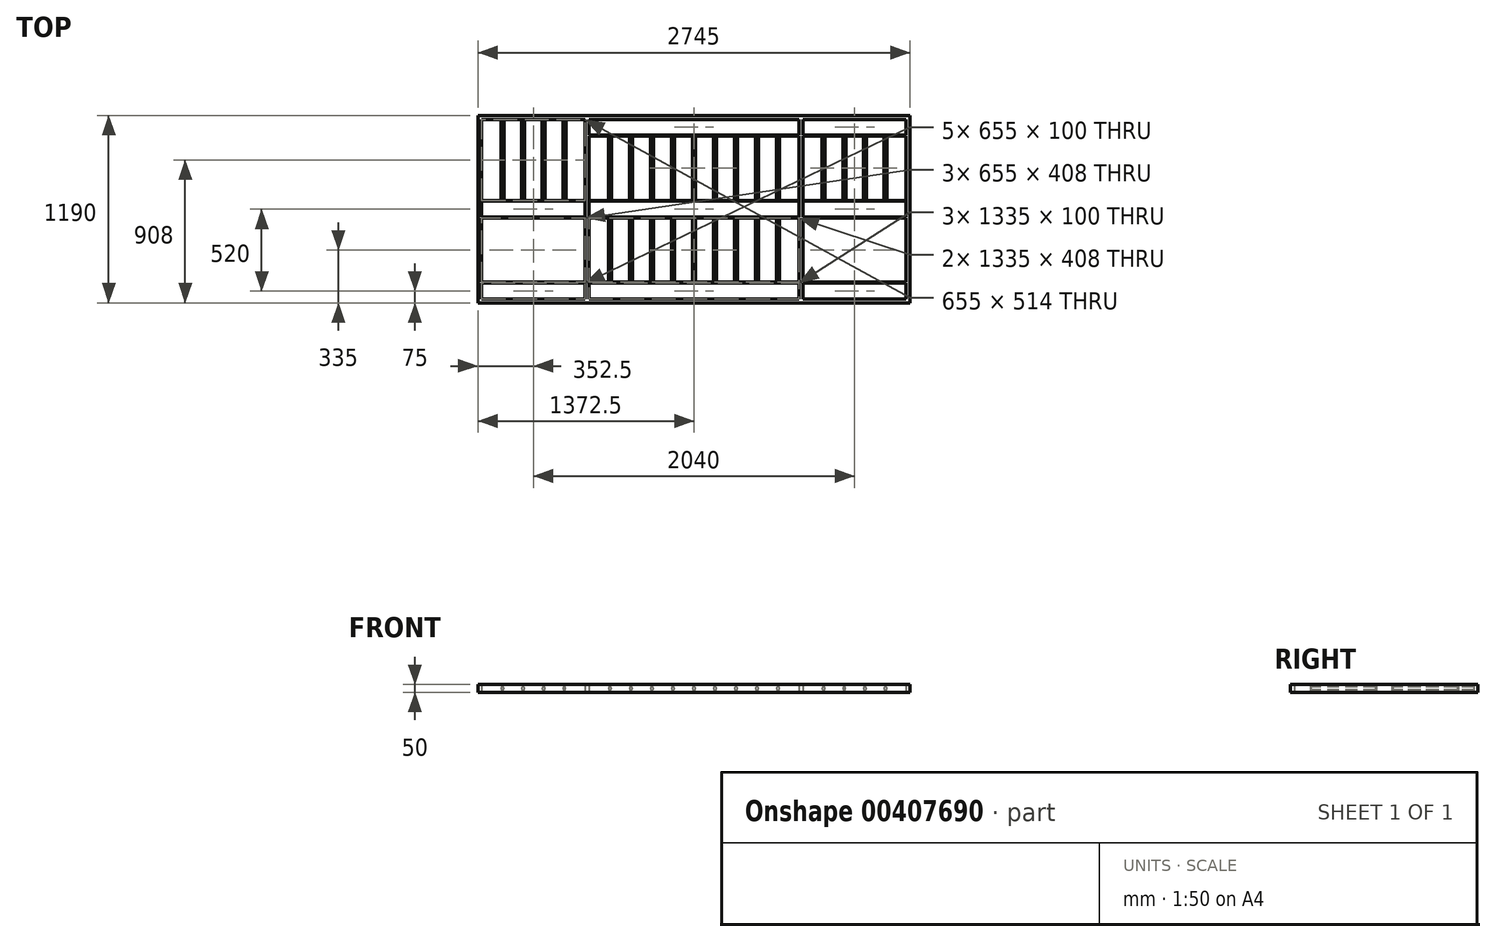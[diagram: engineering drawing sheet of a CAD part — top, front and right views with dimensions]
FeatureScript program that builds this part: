
annotation { "Feature Type Name" : "Feature", "Feature Type Description" : "" }
export const myFeature = defineFeature(function(context is Context, id is Id, definition is map)
    precondition{}
    {
        {
            var Q0;
            Q0=qCreatedBy(makeId("Top.planeOp"),FACE);
            var sketch = newSketch(context, id + "F0", { "sketchPlane" : qUnion([Q0])});
            skLineSegment(sketch, "E0.bottom", {"start": v(0, 0) * mm, "end": v(705, 0) * mm});
            skLineSegment(sketch, "E0.top", {"start": v(0, 1190) * mm, "end": v(705, 1190) * mm});
            skLineSegment(sketch, "E0.left", {"start": v(0, 0) * mm, "end": v(0, 1190) * mm});
            skLineSegment(sketch, "E0.right", {"start": v(705, 0) * mm, "end": v(705, 1190) * mm});
            skLineSegment(sketch, "E1.0", {"start": v(25, 1165) * mm, "end": v(680, 1165) * mm});
            skLineSegment(sketch, "E1.1", {"start": v(25, 25) * mm, "end": v(25, 1165) * mm});
            skLineSegment(sketch, "E1.2", {"start": v(25, 25) * mm, "end": v(680, 25) * mm});
            skLineSegment(sketch, "E1.3", {"start": v(680, 25) * mm, "end": v(680, 1165) * mm});
            skLineSegment(sketch, "E2", {"start": v(759.37, 595) * mm, "end": v(-360.82, 595) * mm, "construction": true});
            skLineSegment(sketch, "E3.bottom", {"start": v(25, 125) * mm, "end": v(680, 125) * mm});
            skLineSegment(sketch, "E3.top", {"start": v(25, 131) * mm, "end": v(680, 131) * mm});
            skLineSegment(sketch, "E3.left", {"start": v(25, 125) * mm, "end": v(25, 131) * mm});
            skLineSegment(sketch, "E3.right", {"start": v(680, 125) * mm, "end": v(680, 131) * mm});
            skLineSegment(sketch, "E4.bottom", {"start": v(25, 545) * mm, "end": v(680, 545) * mm});
            skLineSegment(sketch, "E4.top", {"start": v(25, 539) * mm, "end": v(680, 539) * mm});
            skLineSegment(sketch, "E4.left", {"start": v(25, 545) * mm, "end": v(25, 539) * mm});
            skLineSegment(sketch, "E4.right", {"start": v(680, 545) * mm, "end": v(680, 539) * mm});
            skLineSegment(sketch, "E5.MirrorCS", {"start": v(25, 645) * mm, "end": v(680, 645) * mm});
            skLineSegment(sketch, "E6.MirrorCS", {"start": v(25, 651) * mm, "end": v(680, 651) * mm});
            skLineSegment(sketch, "E7.MirrorCS", {"start": v(25, 1065) * mm, "end": v(25, 1059) * mm});
            skLineSegment(sketch, "E8.MirrorCS", {"start": v(680, 1065) * mm, "end": v(680, 1059) * mm});
            skLineSegment(sketch, "E9.MirrorCS", {"start": v(25, 1059) * mm, "end": v(680, 1059) * mm});
            skLineSegment(sketch, "E10.MirrorCS", {"start": v(25, 1065) * mm, "end": v(680, 1065) * mm});
            skLineSegment(sketch, "E11.1.0.0", {"start": v(705, 1165) * mm, "end": v(1360, 1165) * mm});
            skLineSegment(sketch, "E11.1.0.1", {"start": v(705, 1065) * mm, "end": v(1360, 1065) * mm});
            skLineSegment(sketch, "E11.1.0.2", {"start": v(680, 1190) * mm, "end": v(1385, 1190) * mm});
            skLineSegment(sketch, "E11.1.0.3", {"start": v(705, 545) * mm, "end": v(1360, 545) * mm});
            skLineSegment(sketch, "E11.1.0.4", {"start": v(705, 131) * mm, "end": v(1360, 131) * mm});
            skLineSegment(sketch, "E11.1.0.5", {"start": v(705, 651) * mm, "end": v(1360, 651) * mm});
            skLineSegment(sketch, "E11.1.0.6", {"start": v(705, 1059) * mm, "end": v(1360, 1059) * mm});
            skLineSegment(sketch, "E11.1.0.7", {"start": v(680, 0) * mm, "end": v(1385, 0) * mm});
            skLineSegment(sketch, "E11.1.0.8", {"start": v(1360, 25) * mm, "end": v(1360, 1165) * mm, "construction": true});
            skLineSegment(sketch, "E11.1.0.9", {"start": v(705, 539) * mm, "end": v(1360, 539) * mm});
            skLineSegment(sketch, "E11.1.0.10", {"start": v(705, 125) * mm, "end": v(1360, 125) * mm});
            skLineSegment(sketch, "E11.1.0.11", {"start": v(1439.37, 595) * mm, "end": v(319.18, 595) * mm, "construction": true});
            skLineSegment(sketch, "E11.1.0.12", {"start": v(705, 25) * mm, "end": v(1360, 25) * mm});
            skLineSegment(sketch, "E11.1.0.13", {"start": v(1385, 0) * mm, "end": v(1385, 1190) * mm, "construction": true});
            skLineSegment(sketch, "E11.1.0.14", {"start": v(705, 645) * mm, "end": v(1360, 645) * mm});
            skLineSegment(sketch, "E11.1.0.15", {"start": v(1360, 1065) * mm, "end": v(1360, 1059) * mm});
            skLineSegment(sketch, "E11.1.0.16", {"start": v(1360, 545) * mm, "end": v(1360, 539) * mm});
            skLineSegment(sketch, "E11.1.0.17", {"start": v(1360, 125) * mm, "end": v(1360, 131) * mm});
            skLineSegment(sketch, "E11.2.0.0", {"start": v(1385, 1165) * mm, "end": v(2040, 1165) * mm});
            skLineSegment(sketch, "E11.2.0.1", {"start": v(1385, 1065) * mm, "end": v(2040, 1065) * mm});
            skLineSegment(sketch, "E11.2.0.2", {"start": v(1360, 1190) * mm, "end": v(2065, 1190) * mm});
            skLineSegment(sketch, "E11.2.0.3", {"start": v(1385, 545) * mm, "end": v(2040, 545) * mm});
            skLineSegment(sketch, "E11.2.0.4", {"start": v(1385, 131) * mm, "end": v(2040, 131) * mm});
            skLineSegment(sketch, "E11.2.0.5", {"start": v(1385, 651) * mm, "end": v(2040, 651) * mm});
            skLineSegment(sketch, "E11.2.0.6", {"start": v(1385, 1059) * mm, "end": v(2040, 1059) * mm});
            skLineSegment(sketch, "E11.2.0.7", {"start": v(1360, 0) * mm, "end": v(2065, 0) * mm});
            skLineSegment(sketch, "E11.2.0.8", {"start": v(2040, 25) * mm, "end": v(2040, 1165) * mm});
            skLineSegment(sketch, "E11.2.0.9", {"start": v(1385, 539) * mm, "end": v(2040, 539) * mm});
            skLineSegment(sketch, "E11.2.0.10", {"start": v(1385, 125) * mm, "end": v(2040, 125) * mm});
            skLineSegment(sketch, "E11.2.0.11", {"start": v(2119.37, 595) * mm, "end": v(999.18, 595) * mm, "construction": true});
            skLineSegment(sketch, "E11.2.0.12", {"start": v(1385, 25) * mm, "end": v(2040, 25) * mm});
            skLineSegment(sketch, "E11.2.0.13", {"start": v(2065, 0) * mm, "end": v(2065, 1190) * mm});
            skLineSegment(sketch, "E11.2.0.14", {"start": v(1385, 645) * mm, "end": v(2040, 645) * mm});
            skLineSegment(sketch, "E11.2.0.15", {"start": v(2040, 1065) * mm, "end": v(2040, 1059) * mm});
            skLineSegment(sketch, "E11.2.0.16", {"start": v(2040, 545) * mm, "end": v(2040, 539) * mm});
            skLineSegment(sketch, "E11.2.0.17", {"start": v(2040, 125) * mm, "end": v(2040, 131) * mm});
            skLineSegment(sketch, "E11.direction1", {"start": v(0, 0) * mm, "end": v(680, 0) * mm, "construction": true});
            skLineSegment(sketch, "E12.0.3.0", {"start": v(2065, 1165) * mm, "end": v(2720, 1165) * mm});
            skLineSegment(sketch, "E12.3.3.0", {"start": v(2065, 1065) * mm, "end": v(2720, 1065) * mm});
            skLineSegment(sketch, "E12.6.3.0", {"start": v(2040, 1190) * mm, "end": v(2745, 1190) * mm});
            skLineSegment(sketch, "E12.9.3.0", {"start": v(2065, 545) * mm, "end": v(2720, 545) * mm});
            skLineSegment(sketch, "E12.12.3.0", {"start": v(2065, 131) * mm, "end": v(2720, 131) * mm});
            skLineSegment(sketch, "E12.15.3.0", {"start": v(2065, 651) * mm, "end": v(2720, 651) * mm});
            skLineSegment(sketch, "E12.18.3.0", {"start": v(2065, 1059) * mm, "end": v(2720, 1059) * mm});
            skLineSegment(sketch, "E12.21.3.0", {"start": v(2040, 0) * mm, "end": v(2745, 0) * mm});
            skLineSegment(sketch, "E12.24.3.0", {"start": v(2720, 25) * mm, "end": v(2720, 1165) * mm});
            skLineSegment(sketch, "E12.27.3.0", {"start": v(2065, 539) * mm, "end": v(2720, 539) * mm});
            skLineSegment(sketch, "E12.30.3.0", {"start": v(2065, 125) * mm, "end": v(2720, 125) * mm});
            skLineSegment(sketch, "E12.33.3.0", {"start": v(2799.37, 595) * mm, "end": v(1679.18, 595) * mm, "construction": true});
            skLineSegment(sketch, "E12.36.3.0", {"start": v(2065, 25) * mm, "end": v(2720, 25) * mm});
            skLineSegment(sketch, "E12.39.3.0", {"start": v(2745, 0) * mm, "end": v(2745, 1190) * mm});
            skLineSegment(sketch, "E12.42.3.0", {"start": v(2065, 645) * mm, "end": v(2720, 645) * mm});
            skLineSegment(sketch, "E12.45.3.0", {"start": v(2720, 1065) * mm, "end": v(2720, 1059) * mm});
            skLineSegment(sketch, "E12.48.3.0", {"start": v(2720, 545) * mm, "end": v(2720, 539) * mm});
            skLineSegment(sketch, "E12.51.3.0", {"start": v(2720, 125) * mm, "end": v(2720, 131) * mm});
            skLineSegment(sketch, "E13.bottom", {"start": v(1360, 539) * mm, "end": v(1385, 539) * mm});
            skLineSegment(sketch, "E13.top", {"start": v(1360, 545) * mm, "end": v(1385, 545) * mm});
            skLineSegment(sketch, "E13.left", {"start": v(1360, 539) * mm, "end": v(1360, 545) * mm});
            skLineSegment(sketch, "E13.right", {"start": v(1385, 539) * mm, "end": v(1385, 545) * mm});
            skLineSegment(sketch, "E14.bottom", {"start": v(1360, 125) * mm, "end": v(1385, 125) * mm});
            skLineSegment(sketch, "E14.top", {"start": v(1360, 131) * mm, "end": v(1385, 131) * mm});
            skLineSegment(sketch, "E14.right", {"start": v(1385, 125) * mm, "end": v(1385, 131) * mm});
            skLineSegment(sketch, "E15.bottom", {"start": v(1385, 1065) * mm, "end": v(1360, 1065) * mm});
            skLineSegment(sketch, "E15.top", {"start": v(1385, 1059) * mm, "end": v(1360, 1059) * mm});
            skLineSegment(sketch, "E15.left", {"start": v(1385, 1065) * mm, "end": v(1385, 1059) * mm});
            skLineSegment(sketch, "E16.bottom", {"start": v(1385, 645) * mm, "end": v(1360, 645) * mm});
            skLineSegment(sketch, "E16.top", {"start": v(1385, 651) * mm, "end": v(1360, 651) * mm});
            skLineSegment(sketch, "E16.left", {"start": v(1385, 645) * mm, "end": v(1385, 651) * mm});
            skLineSegment(sketch, "E16.right", {"start": v(1360, 645) * mm, "end": v(1360, 651) * mm});
            skLineSegment(sketch, "E17", {"start": v(1360, 1165) * mm, "end": v(1385, 1165) * mm});
            skLineSegment(sketch, "E18", {"start": v(1360, 25) * mm, "end": v(1385, 25) * mm});
            skSolve(sketch);
        }
        {
            var Q0;
            Q0=qSketchRegion(id+"F0",true);
            var Q1;
            Q1=makeQuery(id+"F0.imprint","IMPRINT",FACE,{"disambiguationData":[TD([[makeQuery(id+"F0.imprint","IMPRINT",EDGE,{"derivedFrom":sQuery(id+"F0.wireOp",EDGE,"E4.bottom")}),-1.0]])]});
            var Q2;
            Q2=makeQuery(id+"F0.imprint","IMPRINT",FACE,{"disambiguationData":[TD([[makeQuery(id+"F0.imprint","IMPRINT",EDGE,{"derivedFrom":sQuery(id+"F0.wireOp",EDGE,"baab227e-6a5d-40b9-91ee-7446e1ab67f20.MirrorCS")}),1.0]])]});
            var Q3;
            Q3=makeQuery(id+"F0.imprint","IMPRINT",FACE,{"disambiguationData":[TD([[makeQuery(id+"F0.imprint","IMPRINT",EDGE,{"derivedFrom":sQuery(id+"F0.wireOp",EDGE,"E3.bottom")}),1.0]])]});
            var Q4;
            Q4=makeQuery(id+"F0.imprint","IMPRINT",FACE,{"disambiguationData":[TD([[makeQuery(id+"F0.imprint","IMPRINT",EDGE,{"derivedFrom":sQuery(id+"F0.wireOp",EDGE,"TbBb99Yr-0gyQ-v6ej-gQRB-Bgt5jI2MECaT.bottom")}),-1.0]])]});
            var Q5;
            Q5=makeQuery(id+"F0.imprint","IMPRINT",FACE,{"disambiguationData":[TD([[makeQuery(id+"F0.imprint","IMPRINT",EDGE,{"derivedFrom":sQuery(id+"F0.wireOp",EDGE,"NzViuoU3-R4T5-xjC5-rI0y-QMhb7gm5c65x.bottom")}),-1.0]])]});
            var Q6;
            Q6=makeQuery(id+"F0.imprint","IMPRINT",FACE,{"disambiguationData":[TD([[makeQuery(id+"F0.imprint","IMPRINT",EDGE,{"derivedFrom":sQuery(id+"F0.wireOp",EDGE,"baab227e-6a5d-40b9-91ee-7446e1ab67f23.MirrorCS")}),-1.0]])]});
            var Q7;
            Q7=makeQuery(id+"F0.imprint","IMPRINT",FACE,{"disambiguationData":[TD([[makeQuery(id+"F0.imprint","IMPRINT",EDGE,{"derivedFrom":sQuery(id+"F0.wireOp",EDGE,"baab227e-6a5d-40b9-91ee-7446e1ab67f22.MirrorCS")}),-1.0]])]});
            var Q8;
            Q8=makeQuery(id+"F0.imprint","IMPRINT",FACE,{"disambiguationData":[TD([[makeQuery(id+"F0.imprint","IMPRINT",EDGE,{"derivedFrom":sQuery(id+"F0.wireOp",EDGE,"baab227e-6a5d-40b9-91ee-7446e1ab67f21.MirrorCS")}),1.0]])]});
            var Q9;
            {var subQ0=sQuery(id+"F0.wireOp",EDGE,"E5.MirrorCS");Q9=makeQuery(id+"F0.imprint","IMPRINT",FACE,{"disambiguationData":[TD([[makeQuery(id+"F0.imprint","IMPRINT",EDGE,{"derivedFrom":subQ0}),1.0]])]});}
            var Q10;
            Q10=makeQuery(id+"F0.imprint","IMPRINT",FACE,{"disambiguationData":[TD([[makeQuery(id+"F0.imprint","IMPRINT",EDGE,{"derivedFrom":sQuery(id+"F0.wireOp",EDGE,"E7.MirrorCS")}),1.0]])]});
            var Q11;
            {var subQ0=sQuery(id+"F0.wireOp",EDGE,"E11.1.0.5");Q11=makeQuery(id+"F0.imprint","IMPRINT",FACE,{"disambiguationData":[TD([[makeQuery(id+"F0.imprint","IMPRINT",EDGE,{"derivedFrom":subQ0}),-1.0]])]});}
            var Q12;
            {var subQ0=sQuery(id+"F0.wireOp",EDGE,"E11.2.0.5");Q12=makeQuery(id+"F0.imprint","IMPRINT",FACE,{"disambiguationData":[TD([[makeQuery(id+"F0.imprint","IMPRINT",EDGE,{"derivedFrom":subQ0}),-1.0]])]});}
            var Q13;
            {var subQ0=sQuery(id+"F0.wireOp",EDGE,"E11.2.0.3");Q13=makeQuery(id+"F0.imprint","IMPRINT",FACE,{"disambiguationData":[TD([[makeQuery(id+"F0.imprint","IMPRINT",EDGE,{"derivedFrom":subQ0}),-1.0]])]});}
            var Q14;
            {var subQ0=sQuery(id+"F0.wireOp",EDGE,"E11.1.0.3");Q14=makeQuery(id+"F0.imprint","IMPRINT",FACE,{"disambiguationData":[TD([[makeQuery(id+"F0.imprint","IMPRINT",EDGE,{"derivedFrom":subQ0}),-1.0]])]});}
            var Q15;
            {var subQ0=sQuery(id+"F0.wireOp",EDGE,"E12.9.3.0");Q15=makeQuery(id+"F0.imprint","IMPRINT",FACE,{"disambiguationData":[TD([[makeQuery(id+"F0.imprint","IMPRINT",EDGE,{"derivedFrom":subQ0}),-1.0]])]});}
            var Q16;
            {var subQ0=sQuery(id+"F0.wireOp",EDGE,"E12.15.3.0");Q16=makeQuery(id+"F0.imprint","IMPRINT",FACE,{"disambiguationData":[TD([[makeQuery(id+"F0.imprint","IMPRINT",EDGE,{"derivedFrom":subQ0}),-1.0]])]});}
            var Q17;
            {var subQ0=sQuery(id+"F0.wireOp",EDGE,"E12.3.3.0");Q17=makeQuery(id+"F0.imprint","IMPRINT",FACE,{"disambiguationData":[TD([[makeQuery(id+"F0.imprint","IMPRINT",EDGE,{"derivedFrom":subQ0}),-1.0]])]});}
            var Q18;
            {var subQ0=sQuery(id+"F0.wireOp",EDGE,"E11.2.0.1");Q18=makeQuery(id+"F0.imprint","IMPRINT",FACE,{"disambiguationData":[TD([[makeQuery(id+"F0.imprint","IMPRINT",EDGE,{"derivedFrom":subQ0}),-1.0]])]});}
            var Q19;
            {var subQ0=sQuery(id+"F0.wireOp",EDGE,"E11.1.0.1");Q19=makeQuery(id+"F0.imprint","IMPRINT",FACE,{"disambiguationData":[TD([[makeQuery(id+"F0.imprint","IMPRINT",EDGE,{"derivedFrom":subQ0}),-1.0]])]});}
            var Q20;
            {var subQ0=sQuery(id+"F0.wireOp",EDGE,"E12.12.3.0");Q20=makeQuery(id+"F0.imprint","IMPRINT",FACE,{"disambiguationData":[TD([[makeQuery(id+"F0.imprint","IMPRINT",EDGE,{"derivedFrom":subQ0}),-1.0]])]});}
            var Q21;
            {var subQ0=sQuery(id+"F0.wireOp",EDGE,"E11.1.0.4");Q21=makeQuery(id+"F0.imprint","IMPRINT",FACE,{"disambiguationData":[TD([[makeQuery(id+"F0.imprint","IMPRINT",EDGE,{"derivedFrom":subQ0}),-1.0]])]});}
            var Q22;
            {var subQ0=sQuery(id+"F0.wireOp",EDGE,"E11.2.0.4");Q22=makeQuery(id+"F0.imprint","IMPRINT",FACE,{"disambiguationData":[TD([[makeQuery(id+"F0.imprint","IMPRINT",EDGE,{"derivedFrom":subQ0}),-1.0]])]});}
            var Q23;
            Q23=makeQuery(id+"F0.imprint","IMPRINT",FACE,{"disambiguationData":[TD([[makeQuery(id+"F0.imprint","IMPRINT",EDGE,{"derivedFrom":sQuery(id+"F0.wireOp",EDGE,"E14.bottom")}),1.0]])]});
            var Q24;
            Q24=makeQuery(id+"F0.imprint","IMPRINT",FACE,{"disambiguationData":[TD([[makeQuery(id+"F0.imprint","IMPRINT",EDGE,{"derivedFrom":sQuery(id+"F0.wireOp",EDGE,"E13.bottom")}),1.0]])]});
            var Q25;
            Q25=makeQuery(id+"F0.imprint","IMPRINT",FACE,{"disambiguationData":[TD([[makeQuery(id+"F0.imprint","IMPRINT",EDGE,{"derivedFrom":sQuery(id+"F0.wireOp",EDGE,"E15.bottom")}),1.0]])]});
            var Q26;
            Q26=makeQuery(id+"F0.imprint","IMPRINT",FACE,{"disambiguationData":[TD([[makeQuery(id+"F0.imprint","IMPRINT",EDGE,{"derivedFrom":sQuery(id+"F0.wireOp",EDGE,"E16.bottom")}),-1.0]])]});
            extrude(context, id + "F1", {"entities" : qUnion([Q0, Q1, Q2, Q3, Q4, Q5, Q6, Q7, Q8, Q9, Q10, Q11, Q12, Q13, Q14, Q15, Q16, Q17, Q18, Q19, Q20, Q21, Q22, Q23, Q24, Q25, Q26]), "depth" : 50 * mm});
        }
        {
            var Q0;
            Q0=makeQuery(id+"F1.opExtrude","SWEPT_FACE",FACE,{"disambiguationData":[OSD([sQuery(id+"F0.wireOp",EDGE,"E3.top")])]});
            var sketch = newSketch(context, id + "F2", { "sketchPlane" : qUnion([Q0])});
            skLineSegment(sketch, "E19", {"start": v(-25, 25) * mm, "end": v(-680, 25) * mm, "construction": true});
            skCircle(sketch, "E20", {"center": v(-156, 25) * mm, "radius": 9.53 * mm});
            skCircle(sketch, "E21.1.0.0", {"center": v(-287, 25) * mm, "radius": 9.53 * mm});
            skCircle(sketch, "E21.2.0.0", {"center": v(-418, 25) * mm, "radius": 9.53 * mm});
            skCircle(sketch, "E21.3.0.0", {"center": v(-549, 25) * mm, "radius": 9.53 * mm});
            skLineSegment(sketch, "E21.direction1", {"start": v(-156, 25) * mm, "end": v(-287, 25) * mm, "construction": true});
            skLineSegment(sketch, "E22", {"start": v(-680, 25) * mm, "end": v(-2065, 25) * mm, "construction": true});
            skLineSegment(sketch, "E23", {"start": v(-1372.5, 25) * mm, "end": v(-1372.5, 237.59) * mm, "construction": true});
            skCircle(sketch, "E24.MirrorC", {"center": v(-2589, 25) * mm, "radius": 9.53 * mm});
            skCircle(sketch, "E25.MirrorC", {"center": v(-2458, 25) * mm, "radius": 9.53 * mm});
            skCircle(sketch, "E26.MirrorC", {"center": v(-2327, 25) * mm, "radius": 9.53 * mm});
            skCircle(sketch, "E27.MirrorC", {"center": v(-2196, 25) * mm, "radius": 9.53 * mm});
            skSolve(sketch);
        }
        {
            var Q0;
            Q0=sQuery(id+"F2.wireOp",EDGE,"E21.2.0.0");
            var Q1;
            Q1=sQuery(id+"F2.wireOp",EDGE,"E21.3.0.0");
            var Q2;
            Q2=sQuery(id+"F2.wireOp",EDGE,"E26.MirrorC");
            var Q3;
            Q3=sQuery(id+"F2.wireOp",EDGE,"E21.1.0.0");
            var Q4;
            Q4=sQuery(id+"F2.wireOp",EDGE,"E25.MirrorC");
            var Q5;
            Q5=sQuery(id+"F2.wireOp",EDGE,"E20");
            var Q6;
            Q6=sQuery(id+"F2.wireOp",EDGE,"E27.MirrorC");
            var Q7;
            Q7=sQuery(id+"F2.wireOp",EDGE,"E24.MirrorC");
            extrude(context, id + "F3", {"bodyType" : ToolBodyType.SURFACE, "surfaceEntities" : qUnion([Q0, Q1, Q2, Q3, Q4, Q5, Q6, Q7]), "endBound" : BoundingType.UP_TO_NEXT, "depth" : 25 * mm});
        }
        {
            var Q0;
            Q0=makeQuery(id+"F1.opExtrude","SWEPT_FACE",FACE,{"disambiguationData":[OSD([sQuery(id+"F0.wireOp",EDGE,"E6.MirrorCS")])]});
            var sketch = newSketch(context, id + "F4", { "sketchPlane" : qUnion([Q0])});
            skLineSegment(sketch, "E28", {"start": v(-25, 25) * mm, "end": v(-680, 25) * mm, "construction": true});
            skLineSegment(sketch, "E29", {"start": v(-680, 25) * mm, "end": v(-2065, 25) * mm, "construction": true});
            skCircle(sketch, "E30", {"center": v(-156, 25) * mm, "radius": 9.53 * mm});
            skCircle(sketch, "E31.1.0.0", {"center": v(-287, 25) * mm, "radius": 9.53 * mm});
            skCircle(sketch, "E31.2.0.0", {"center": v(-418, 25) * mm, "radius": 9.53 * mm});
            skCircle(sketch, "E31.3.0.0", {"center": v(-549, 25) * mm, "radius": 9.53 * mm});
            skLineSegment(sketch, "E31.direction1", {"start": v(-156, 25) * mm, "end": v(-287, 25) * mm, "construction": true});
            skLineSegment(sketch, "E32", {"start": v(-1372.5, 25) * mm, "end": v(-1372.5, -85.74) * mm, "construction": true});
            skPoint(sketch, "E32.endSnap0", {"position": v(-1372.5, 25) * mm});
            skCircle(sketch, "E33.MirrorC", {"center": v(-2196, 25) * mm, "radius": 9.53 * mm});
            skCircle(sketch, "E34.MirrorC", {"center": v(-2327, 25) * mm, "radius": 9.53 * mm});
            skCircle(sketch, "E35.MirrorC", {"center": v(-2458, 25) * mm, "radius": 9.53 * mm});
            skCircle(sketch, "E36.MirrorC", {"center": v(-2589, 25) * mm, "radius": 9.53 * mm});
            skSolve(sketch);
        }
        {
            var Q0;
            Q0 = qSketchRegion(id + "F4", true);
            extrude(context, id + "F5", {"entities" : qUnion([Q0]), "operationType" : NewBodyOperationType.ADD, "endBound" : BoundingType.UP_TO_NEXT, "depth" : 25 * mm});
        }
        {
            var Q0;
            Q0=makeQuery(id+"F1.opExtrude","SWEPT_FACE",FACE,{"disambiguationData":[OSD([sQuery(id+"F0.wireOp",EDGE,"E11.1.0.4"),sQuery(id+"F0.wireOp",EDGE,"E11.2.0.4"),sQuery(id+"F0.wireOp",EDGE,"E14.top")])]});
            var sketch = newSketch(context, id + "F6", { "sketchPlane" : qUnion([Q0])});
            skLineSegment(sketch, "E37", {"start": v(-705, 25) * mm, "end": v(-2040, 25) * mm, "construction": true});
            skCircle(sketch, "E38", {"center": v(-838.5, 25) * mm, "radius": 9.53 * mm});
            skCircle(sketch, "E39.1.0.0", {"center": v(-972, 25) * mm, "radius": 9.53 * mm});
            skCircle(sketch, "E39.2.0.0", {"center": v(-1105.5, 25) * mm, "radius": 9.53 * mm});
            skCircle(sketch, "E39.3.0.0", {"center": v(-1239, 25) * mm, "radius": 9.53 * mm});
            skCircle(sketch, "E39.4.0.0", {"center": v(-1372.5, 25) * mm, "radius": 9.53 * mm});
            skCircle(sketch, "E39.5.0.0", {"center": v(-1506, 25) * mm, "radius": 9.53 * mm});
            skCircle(sketch, "E39.6.0.0", {"center": v(-1639.5, 25) * mm, "radius": 9.53 * mm});
            skCircle(sketch, "E39.7.0.0", {"center": v(-1773, 25) * mm, "radius": 9.53 * mm});
            skCircle(sketch, "E39.8.0.0", {"center": v(-1906.5, 25) * mm, "radius": 9.53 * mm});
            skLineSegment(sketch, "E39.direction1", {"start": v(-838.5, 25) * mm, "end": v(-972, 25) * mm, "construction": true});
            skSolve(sketch);
        }
        {
            var Q0;
            Q0 = qSketchRegion(id + "F6", true);
            extrude(context, id + "F7", {"entities" : qUnion([Q0]), "operationType" : NewBodyOperationType.ADD, "endBound" : BoundingType.UP_TO_NEXT, "depth" : 25 * mm});
        }
        {
            var Q0;
            Q0=makeQuery(id+"F1.opExtrude","SWEPT_FACE",FACE,{"disambiguationData":[OSD([sQuery(id+"F0.wireOp",EDGE,"E11.1.0.5"),sQuery(id+"F0.wireOp",EDGE,"E11.2.0.5"),sQuery(id+"F0.wireOp",EDGE,"E16.top")])]});
            var sketch = newSketch(context, id + "F8", { "sketchPlane" : qUnion([Q0])});
            skLineSegment(sketch, "E40", {"start": v(-705, 25) * mm, "end": v(-2040, 25) * mm, "construction": true});
            skCircle(sketch, "E41", {"center": v(-838.5, 25) * mm, "radius": 9.53 * mm});
            skCircle(sketch, "E42.1.0.0", {"center": v(-972, 25) * mm, "radius": 9.53 * mm});
            skCircle(sketch, "E42.2.0.0", {"center": v(-1105.5, 25) * mm, "radius": 9.53 * mm});
            skCircle(sketch, "E42.3.0.0", {"center": v(-1239, 25) * mm, "radius": 9.53 * mm});
            skCircle(sketch, "E42.4.0.0", {"center": v(-1372.5, 25) * mm, "radius": 9.53 * mm});
            skCircle(sketch, "E42.5.0.0", {"center": v(-1506, 25) * mm, "radius": 9.53 * mm});
            skCircle(sketch, "E42.6.0.0", {"center": v(-1639.5, 25) * mm, "radius": 9.53 * mm});
            skCircle(sketch, "E42.7.0.0", {"center": v(-1773, 25) * mm, "radius": 9.53 * mm});
            skCircle(sketch, "E42.8.0.0", {"center": v(-1906.5, 25) * mm, "radius": 9.53 * mm});
            skLineSegment(sketch, "E42.direction1", {"start": v(-838.5, 25) * mm, "end": v(-972, 25) * mm, "construction": true});
            skSolve(sketch);
        }
        {
            var Q0;
            Q0 = qSketchRegion(id + "F8", true);
            extrude(context, id + "F9", {"entities" : qUnion([Q0]), "operationType" : NewBodyOperationType.ADD, "endBound" : BoundingType.UP_TO_NEXT, "depth" : 25 * mm});
        }
    });
